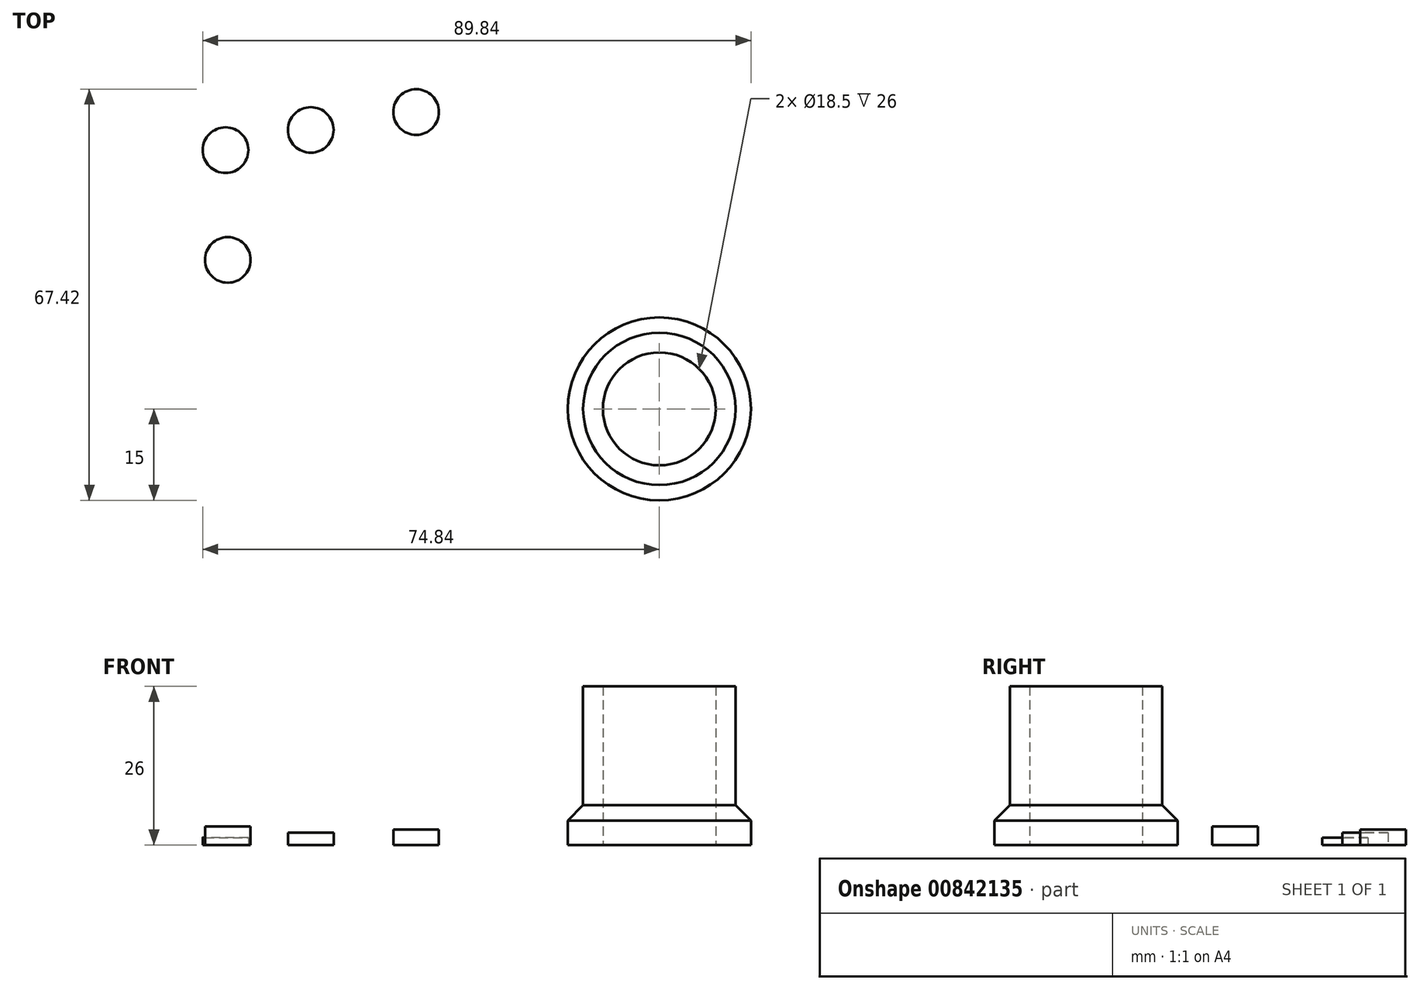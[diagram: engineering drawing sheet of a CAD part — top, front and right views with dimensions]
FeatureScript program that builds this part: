
annotation { "Feature Type Name" : "Feature", "Feature Type Description" : "" }
export const myFeature = defineFeature(function(context is Context, id is Id, definition is map)
    precondition{}
    {
        {
            var Q0;
            Q0=qCreatedBy(makeId("Top.planeOp"),FACE);
            var sketch = newSketch(context, id + "F0", { "sketchPlane" : qUnion([Q0])});
            skCircle(sketch, "E0", {"center": v(-71.1, 42.44) * mm, "radius": 3.74 * mm});
            skSolve(sketch);
        }
        {
            var Q0;
            Q0 = qSketchRegion(id + "F0", true);
            extrude(context, id + "F1", {"entities" : qUnion([Q0]), "depth" : 1.2 * mm, "offsetDistance" : 25 * mm});
        }
        {
            var Q0;
            Q0=qCreatedBy(makeId("Top.planeOp"),FACE);
            var sketch = newSketch(context, id + "F2", { "sketchPlane" : qUnion([Q0])});
            skCircle(sketch, "E1", {"center": v(-57.14, 45.75) * mm, "radius": 3.74 * mm});
            skSolve(sketch);
        }
        {
            var Q0;
            Q0 = qSketchRegion(id + "F2", true);
            extrude(context, id + "F3", {"entities" : qUnion([Q0]), "depth" : 2 * mm, "offsetDistance" : 25 * mm});
        }
        {
            var Q0;
            Q0=qCreatedBy(makeId("Top.planeOp"),FACE);
            var sketch = newSketch(context, id + "F4", { "sketchPlane" : qUnion([Q0])});
            skCircle(sketch, "E2", {"center": v(-39.87, 48.68) * mm, "radius": 3.74 * mm});
            skSolve(sketch);
        }
        {
            var Q0;
            Q0 = qSketchRegion(id + "F4", true);
            extrude(context, id + "F5", {"entities" : qUnion([Q0]), "depth" : 2.5 * mm, "offsetDistance" : 25 * mm});
        }
        {
            var Q0;
            Q0=qCreatedBy(makeId("Top.planeOp"),FACE);
            var sketch = newSketch(context, id + "F6", { "sketchPlane" : qUnion([Q0])});
            skCircle(sketch, "E3", {"center": v(-70.73, 24.43) * mm, "radius": 3.74 * mm});
            skSolve(sketch);
        }
        {
            var Q0;
            Q0 = qSketchRegion(id + "F6", true);
            extrude(context, id + "F7", {"entities" : qUnion([Q0]), "depth" : 3 * mm, "offsetDistance" : 25 * mm});
        }
        {
            var Q0;
            Q0=qCreatedBy(makeId("Top.planeOp"),FACE);
            var sketch = newSketch(context, id + "F8", { "sketchPlane" : qUnion([Q0])});
            skCircle(sketch, "E4", {"center": v(0, 0) * mm, "radius": 15 * mm});
            skCircle(sketch, "E5", {"center": v(0, 0) * mm, "radius": 9.25 * mm});
            skSolve(sketch);
        }
        {
            var Q0;
            Q0 = qSketchRegion(id + "F8", true);
            extrude(context, id + "F9", {"entities" : qUnion([Q0]), "depth" : 26 * mm, "offsetDistance" : 25 * mm});
        }
        {
            var Q0;
            Q0=makeQuery(id+"F9.opExtrude","CAP_FACE",FACE,{"disambiguationData":[OSD([sQuery(id+"F8.wireOp",EDGE,"E4"),sQuery(id+"F8.wireOp",EDGE,"E5")])],"isStart":false});
            var sketch = newSketch(context, id + "F10", { "sketchPlane" : qUnion([Q0])});
            skCircle(sketch, "E6", {"center": v(0, 0) * mm, "radius": 12.5 * mm});
            skCircle(sketch, "E7", {"center": v(0, 0) * mm, "radius": 15 * mm});
            skSolve(sketch);
        }
        {
            var Q0;
            Q0 = qSketchRegion(id + "F10", true);
            extrude(context, id + "F11", {"entities" : qUnion([Q0]), "operationType" : NewBodyOperationType.REMOVE, "oppositeDirection" : true, "depth" : 22 * mm, "offsetDistance" : 25 * mm});
        }
        {
            var Q0;
            Q0=makeQuery(id+"F11.boolean.opBoolean","COPY",EDGE,{"derivedFrom":makeQuery(id+"F11.opExtrude","CAP_EDGE",EDGE,{"disambiguationData":[OSD([sQuery(id+"F10.wireOp",EDGE,"E6")])],"isStart":false})});
            chamfer(context, id + "F12", {"entities" : qUnion([Q0]), "width" : 2.5 * mm, "tangentPropagation" : true});
        }
    });
